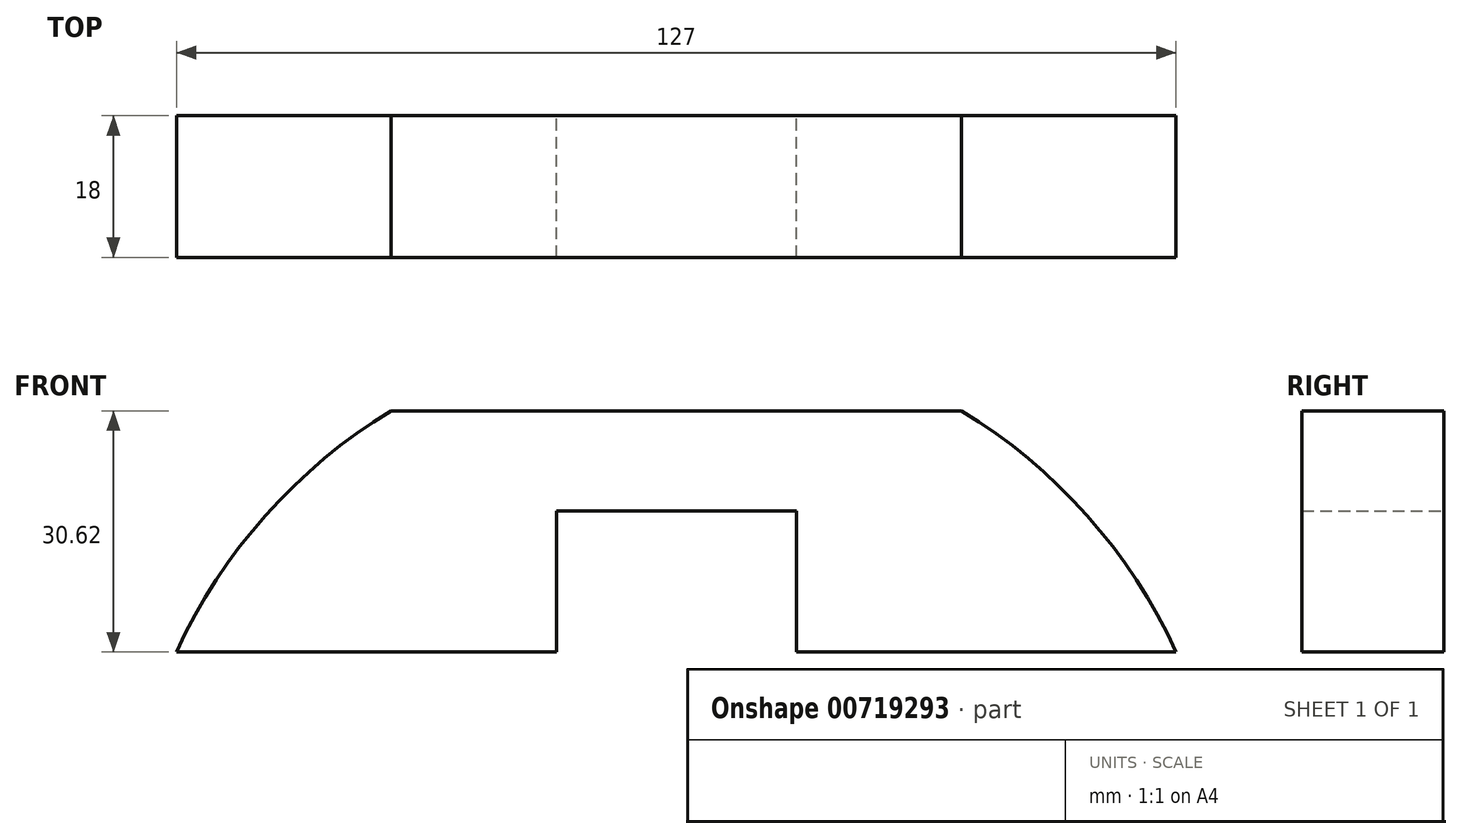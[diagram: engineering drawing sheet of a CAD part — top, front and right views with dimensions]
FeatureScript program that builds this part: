
annotation { "Feature Type Name" : "Feature", "Feature Type Description" : "" }
export const myFeature = defineFeature(function(context is Context, id is Id, definition is map)
    precondition{}
    {
        {
            var Q0;
            Q0=qCreatedBy(makeId("Front.planeOp"),FACE);
            var sketch = newSketch(context, id + "F0", { "sketchPlane" : qUnion([Q0])});
            skLineSegment(sketch, "E0", {"start": v(0, 0) * mm, "end": v(0, 47.02) * mm, "construction": true});
            skLineSegment(sketch, "E1", {"start": v(-63.5, 29.1) * mm, "end": v(-15.24, 29.1) * mm});
            skLineSegment(sketch, "E2", {"start": v(63.5, 29.1) * mm, "end": v(15.24, 29.1) * mm});
            skLineSegment(sketch, "E3", {"start": v(-15.24, 29.1) * mm, "end": v(-15.24, 47.02) * mm});
            skLineSegment(sketch, "E4", {"start": v(-15.24, 47.02) * mm, "end": v(15.24, 47.02) * mm});
            skLineSegment(sketch, "E5", {"start": v(15.24, 29.1) * mm, "end": v(15.24, 47.02) * mm});
            skArc(sketch, "E6", {"start": v(63.5, 29.1) * mm, "mid": v(52.16, 46.46) * mm, "end": v(36.22, 59.72) * mm});
            skLineSegment(sketch, "E7", {"start": v(-36.22, 59.72) * mm, "end": v(36.22, 59.72) * mm});
            skArc(sketch, "E8.trimOffspring", {"start": v(-36.22, 59.72) * mm, "mid": v(-52.16, 46.46) * mm, "end": v(-63.5, 29.1) * mm});
            skSolve(sketch);
        }
        {
            var Q0;
            Q0=makeQuery(id+"F0.imprint","IMPRINT",FACE,{"disambiguationData":[TD([[makeQuery(id+"F0.imprint","IMPRINT",EDGE,{"derivedFrom":sQuery(id+"F0.wireOp",EDGE,"E1")}),1.0]])]});
            extrude(context, id + "F1", {"entities" : qUnion([Q0]), "depth" : 18 * mm, "offsetDistance" : 25.4 * mm});
        }
    });
